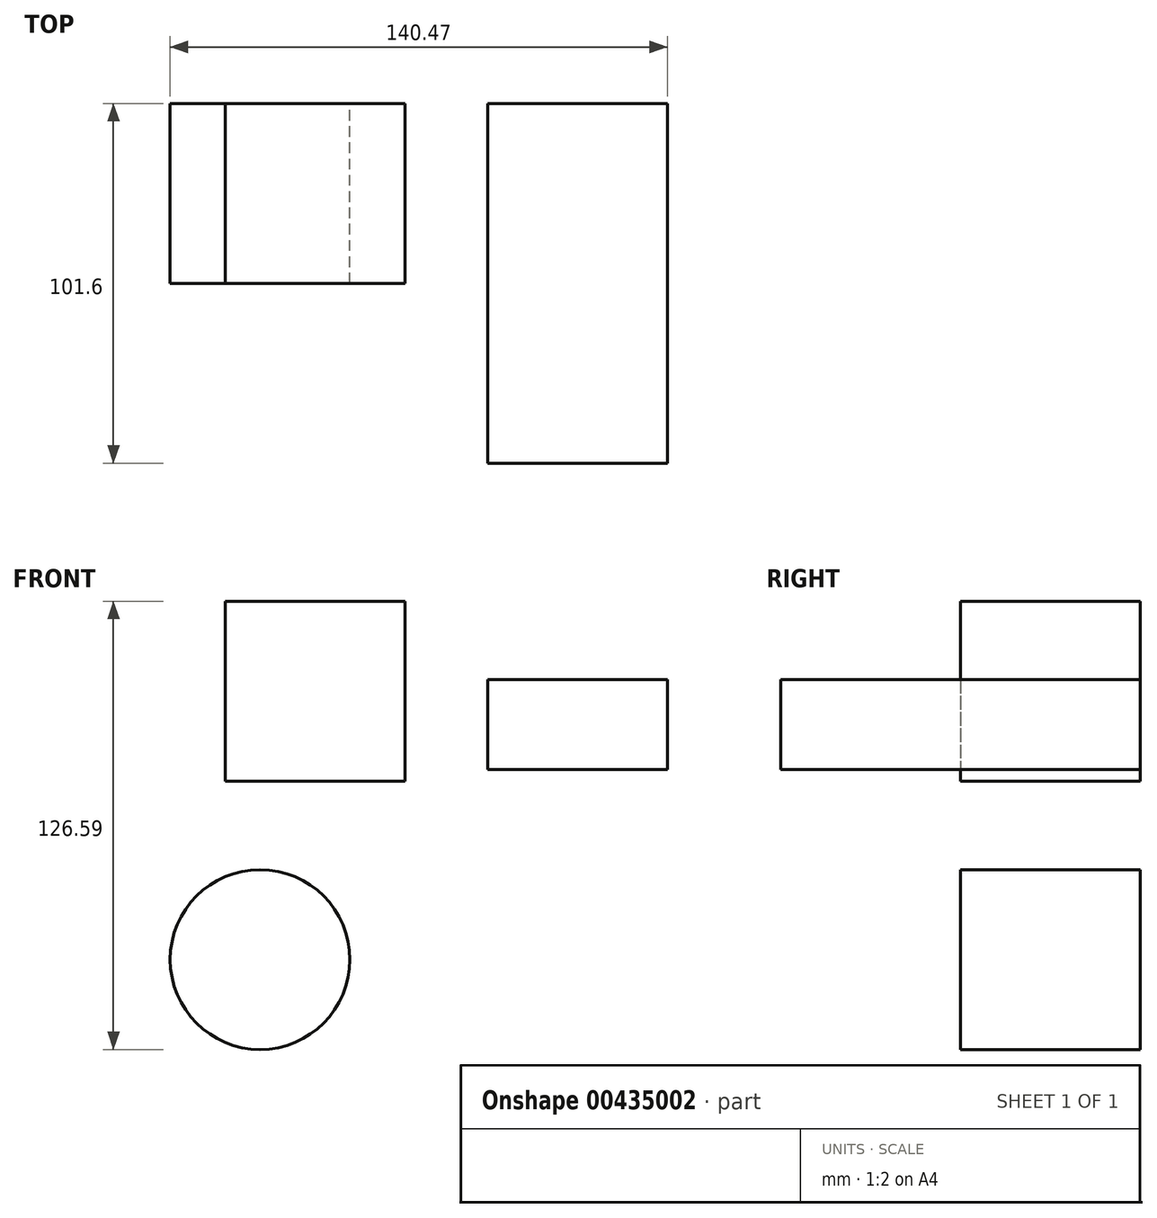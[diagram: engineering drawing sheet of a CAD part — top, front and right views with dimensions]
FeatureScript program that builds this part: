
annotation { "Feature Type Name" : "Feature", "Feature Type Description" : "" }
export const myFeature = defineFeature(function(context is Context, id is Id, definition is map)
    precondition{}
    {
        {
            var Q0;
            Q0=qCreatedBy(makeId("Front.planeOp"),FACE);
            var sketch = newSketch(context, id + "F0", { "sketchPlane" : qUnion([Q0])});
            skLineSegment(sketch, "E0.bottom", {"start": v(-61.92, 67.93) * mm, "end": v(-11.12, 67.93) * mm});
            skLineSegment(sketch, "E0.top", {"start": v(-61.92, 17.13) * mm, "end": v(-11.12, 17.13) * mm});
            skLineSegment(sketch, "E0.left", {"start": v(-61.92, 67.93) * mm, "end": v(-61.92, 17.13) * mm});
            skLineSegment(sketch, "E0.right", {"start": v(-11.12, 67.93) * mm, "end": v(-11.12, 17.13) * mm});
            skSolve(sketch);
        }
        {
            var Q0;
            Q0=qCreatedBy(makeId("Front.planeOp"),FACE);
            var sketch = newSketch(context, id + "F1", { "sketchPlane" : qUnion([Q0])});
            skLineSegment(sketch, "E1.bottom", {"start": v(12.17, 45.84) * mm, "end": v(62.97, 45.84) * mm});
            skLineSegment(sketch, "E1.top", {"start": v(12.17, 20.44) * mm, "end": v(62.97, 20.44) * mm});
            skLineSegment(sketch, "E1.left", {"start": v(12.17, 45.84) * mm, "end": v(12.17, 20.44) * mm});
            skLineSegment(sketch, "E1.right", {"start": v(62.97, 45.84) * mm, "end": v(62.97, 20.44) * mm});
            skSolve(sketch);
        }
        {
            var Q0;
            Q0=qCreatedBy(makeId("Front.planeOp"),FACE);
            var sketch = newSketch(context, id + "F2", { "sketchPlane" : qUnion([Q0])});
            skCircle(sketch, "E2", {"center": v(-52.1, -33.26) * mm, "radius": 25.4 * mm});
            skSolve(sketch);
        }
        {
            var Q0;
            Q0=makeQuery(id+"F0.imprint","IMPRINT",FACE,{"disambiguationData":[TD([[makeQuery(id+"F0.imprint","IMPRINT",EDGE,{"derivedFrom":sQuery(id+"F0.wireOp",EDGE,"E0.bottom")}),-1.0]])]});
            extrude(context, id + "F3", {"entities" : qUnion([Q0]), "depth" : 50.8 * mm});
        }
        {
            var Q0;
            Q0=makeQuery(id+"F1.imprint","IMPRINT",FACE,{"disambiguationData":[TD([[makeQuery(id+"F1.imprint","IMPRINT",EDGE,{"derivedFrom":sQuery(id+"F1.wireOp",EDGE,"E1.bottom")}),-1.0]])]});
            extrude(context, id + "F4", {"entities" : qUnion([Q0]), "depth" : 50.8 * mm});
        }
        {
            var Q0;
            Q0=makeQuery(id+"F4.opExtrude","CAP_FACE",FACE,{"disambiguationData":[OSD([sQuery(id+"F1.wireOp",EDGE,"E1.bottom"),sQuery(id+"F1.wireOp",EDGE,"E1.top"),sQuery(id+"F1.wireOp",EDGE,"E1.left"),sQuery(id+"F1.wireOp",EDGE,"E1.right")])],"isStart":false});
            var Q1;
            Q1=makeQuery(id+"F4.opExtrude","CAP_FACE",FACE,{"disambiguationData":[OSD([sQuery(id+"F1.wireOp",EDGE,"E1.bottom"),sQuery(id+"F1.wireOp",EDGE,"E1.top"),sQuery(id+"F1.wireOp",EDGE,"E1.left"),sQuery(id+"F1.wireOp",EDGE,"E1.right")])],"isStart":true});
            var Q2;
            Q2=makeQuery(id+"F2.imprint","IMPRINT",FACE,{"disambiguationData":[TD([[makeQuery(id+"F2.imprint","IMPRINT",EDGE,{"derivedFrom":sQuery(id+"F2.wireOp",EDGE,"E2")}),1.0]])]});
            extrude(context, id + "F5", {"entities" : qUnion([Q0, Q1, Q2]), "operationType" : NewBodyOperationType.ADD, "depth" : 50.8 * mm});
        }
    });
